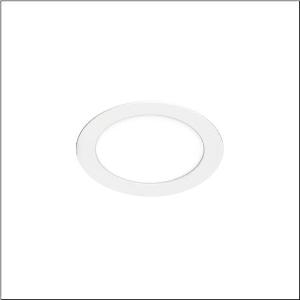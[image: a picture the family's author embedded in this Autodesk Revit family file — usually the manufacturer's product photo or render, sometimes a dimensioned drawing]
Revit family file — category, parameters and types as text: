
# Revit family: lunis_41_flat_51dr107fgca
name_source: partatom
category: Lighting Fixtures
units: mm (PartAtom-declared; Revit-internal decimal feet)

## family parameters
Cut with Voids When Loaded = No
Host = Face
Light Source = No
Part Type = Normal
Room Calculation Point = No
Round Connector Dimension = Use Diameter
Shared = No

## types (1)
- --- (1 x LED, 2160 lm, 22 W, 4000K)
    Apparent Load = 22 VA
    CIE Flux Codes = 49 80 96 100 100
    Color Rendering = 80
    Color Temperature = 4000K
    Default Elevation = 1800 mm
    Description = Lunis 41,  flat, downlight, light emission: direct distribution, LED rated luminous flux: 2.050lm, light colour: 830/840, control gear: ECG, mains connection: 230V, AC, 50/60Hz, housing, round, of aluminium, coated, traffic white (RAL 9016), diameter: 225mm, protection rating (complete): IP20, protection rating (on room side): IP44, insulation class (complete): insulation class II (safety insulation), certification: CE, permissible ambient temperature for indoor applications: -20..+40°C, packaging unit: 1 piece
    Height = 0 mm  [stored 0 ft]
    Lamp = 1 x LED
    Lamp Light Flux = 2160 lm
    Lamp Power = 22 W
    Lamp count = 1
    Length = 225 mm
    Luminous efficacy = 98 lm/W
    Manufacturer = Siteco
    ModVariant = No
    Model = 51DR107FGCA
    Mounting Place = Ceiling
    Mounting Type = Recessed
    Number of Poles = 1
    OnlyDefault = Yes
    Power Factor = 1
    Product Name = Lunis 41 flat
    Product group = downlight
    ProductGroupID = 400
    Protection Class = Protection class II
    Protection Degree = IP 20
    RLX_Detail_Level = 1
    RLX_Emergency_Light_Flux = 0 lm
    RLX_Emergency_Type = 0
    RLX_Emergency_Type_DB = No
    RlxData = <blob elided: 22021 chars, md5=1f3ce3c0>
    Socket = socket
    Standby Power = 0 W
    System Light Flux = 2160 lm
    System Power = 22 W
    Type Comments = factory setting: colour temperature 4000K
    Type Image = l_1007032.jpg
    URL = http://relux.com
    VarID = @adj_130675
    Voltage = 0 V
    Weight = 0.00 kg
    Width = 0 mm  [stored 0 ft]

note: [stored X ft] marks values corroborated as IEEE doubles in the binary element streams (Revit-internal decimal feet)

## geometry (parser evidence)
native form markers: Blend x4, Sweep x11
no freeform markers — native parametric forms only
